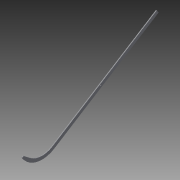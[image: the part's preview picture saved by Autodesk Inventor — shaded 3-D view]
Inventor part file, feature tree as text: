
AUTODESK INVENTOR PART (.ipt)
format: ipt  version: 2013 (Build 170138000, 138)  size: 115,200 bytes
history: native  units: in
note: dims shown in document units (in); Inventor stores cm internally (conversion verified against a paired STEP export)
features: extrude x3, sketch x3
ambient origin geometry x8: Origin, YZ Plane, XZ Plane, XY Plane, X Axis, Y Axis, Z Axis, Center Point
bodies: Solid1 (feature_tree)
feature tree (6):
  extrude  "Extrusion1"  Depth=10.39in
  extrude  "Extrusion2"  Depth=1.0in
  extrude  "Extrusion3"  Depth=3.0in
  sketch  "Sketch1"  dims[d5=12.0in d6=10.39in]
  sketch  "Sketch2"  dims[d7=1.0in d8=1.0in]
  sketch  "Sketch3"  dims[d9=20.0in d10=3.0in d11=5.0in d12=0.5in d13=1.0in d14=1.0in d15=12.0in d16=1.0in d17=0.5in d18=0.25in d19=0.0in d20=0.5in d21=0.25in d22=1.0in d23=0.0in d24=20.0in d25=0.0in]
